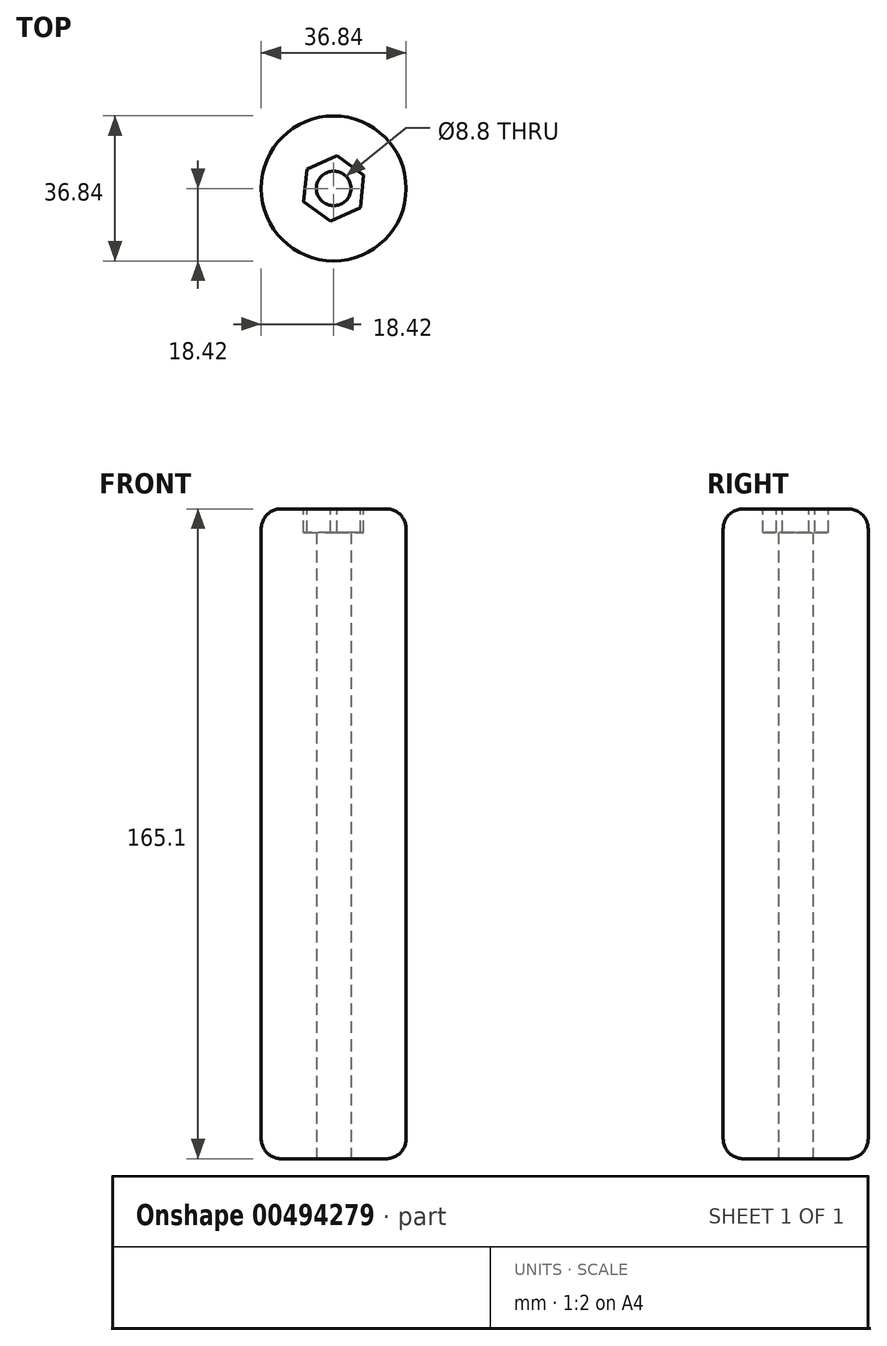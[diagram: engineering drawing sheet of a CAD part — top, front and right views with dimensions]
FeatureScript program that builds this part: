
annotation { "Feature Type Name" : "Feature", "Feature Type Description" : "" }
export const myFeature = defineFeature(function(context is Context, id is Id, definition is map)
    precondition{}
    {
        {
            var Q0;
            Q0=qCreatedBy(makeId("Top.planeOp"),FACE);
            var sketch = newSketch(context, id + "F0", { "sketchPlane" : qUnion([Q0])});
            skCircle(sketch, "E0", {"center": v(0, 0) * mm, "radius": 18.41 * mm});
            skSolve(sketch);
        }
        {
            var Q0;
            Q0=makeQuery(id+"F0.imprint","IMPRINT",FACE,{"disambiguationData":[TD([[makeQuery(id+"F0.imprint","IMPRINT",EDGE,{"derivedFrom":sQuery(id+"F0.wireOp",EDGE,"E0")}),1.0]])]});
            extrude(context, id + "F1", {"entities" : qUnion([Q0]), "depth" : 165.1 * mm});
        }
        {
            var Q0;
            Q0=makeQuery(id+"F1.opExtrude","CAP_EDGE",EDGE,{"disambiguationData":[OSD([sQuery(id+"F0.wireOp",EDGE,"E0")])],"isStart":false});
            var Q1;
            Q1=makeQuery(id+"F1.opExtrude","CAP_EDGE",EDGE,{"disambiguationData":[OSD([sQuery(id+"F0.wireOp",EDGE,"E0")])],"isStart":true});
            fillet(context, id + "F2", {"entities" : qUnion([Q0, Q1]), "radius" : 5.08 * mm, "tangentPropagation" : true, "allowEdgeOverflow" : false});
        }
        {
            var Q0;
            Q0=sQuery(id+"F0.wireOp",VERTEX,"E0.center");
            var Q1;
            Q1=makeQuery(id+"F1.opExtrude","SWEPT_BODY",BODY,{"disambiguationData":[OSD([sQuery(id+"F0.wireOp",EDGE,"E0")])]});
            hole(context, id + "F3", {"style" : HoleStyle.SIMPLE, "endStyle" : HoleEndStyle.THROUGH, "oppositeDirection" : true, "standardTappedOrClearance" : lookupTablePath({ "standard" : "ISO", "fit" : "Normal", "size" : "M8", "type" : "Clearance" }), "standardBlindInLast" : lookupTablePath({ "fit" : "Standard", "standard" : "ISO", "size" : "M8", "type" : "Clearance" }), "holeDiameter" : 8.8 * mm, "isTappedThrough" : true, "tappedDepth" : 12.7 * mm, "tapClearance" : 3, "locations" : qUnion([Q0]), "scope" : qUnion([Q1])});
        }
        {
            var Q0;
            Q0=makeQuery(id+"F1.opExtrude","CAP_FACE",FACE,{"disambiguationData":[OSD([sQuery(id+"F0.wireOp",EDGE,"E0")])],"isStart":false});
            var sketch = newSketch(context, id + "F4", { "sketchPlane" : qUnion([Q0])});
            skPoint(sketch, "E1.0", {"position": v(0, 0) * mm});
            skCircle(sketch, "E2.cCircle", {"center": v(0, 0) * mm, "radius": 7.25 * mm, "construction": true});
            skLineSegment(sketch, "E2.0", {"start": v(-6.79, 4.9) * mm, "end": v(0.85, 8.33) * mm});
            skLineSegment(sketch, "E2.1", {"start": v(0.85, 8.33) * mm, "end": v(7.64, 3.42) * mm});
            skLineSegment(sketch, "E2.2", {"start": v(7.64, 3.42) * mm, "end": v(6.79, -4.9) * mm});
            skLineSegment(sketch, "E2.3", {"start": v(6.79, -4.9) * mm, "end": v(-0.85, -8.33) * mm});
            skLineSegment(sketch, "E2.4", {"start": v(-0.85, -8.33) * mm, "end": v(-7.64, -3.42) * mm});
            skLineSegment(sketch, "E2.5", {"start": v(-7.64, -3.42) * mm, "end": v(-6.79, 4.9) * mm});
            skPoint(sketch, "E2.0.midPoint", {"position": v(-2.97, 6.62) * mm});
            skSolve(sketch);
        }
        {
            var Q0;
            Q0=makeQuery(id+"F4.imprint","IMPRINT",FACE,{"disambiguationData":[TD([[makeQuery(id+"F4.imprint","IMPRINT",EDGE,{"derivedFrom":sQuery(id+"F4.wireOp",EDGE,"E2.0")}),-1.0]])]});
            extrude(context, id + "F5", {"entities" : qUnion([Q0]), "operationType" : NewBodyOperationType.REMOVE, "oppositeDirection" : true, "depth" : 6 * mm});
        }
    });
